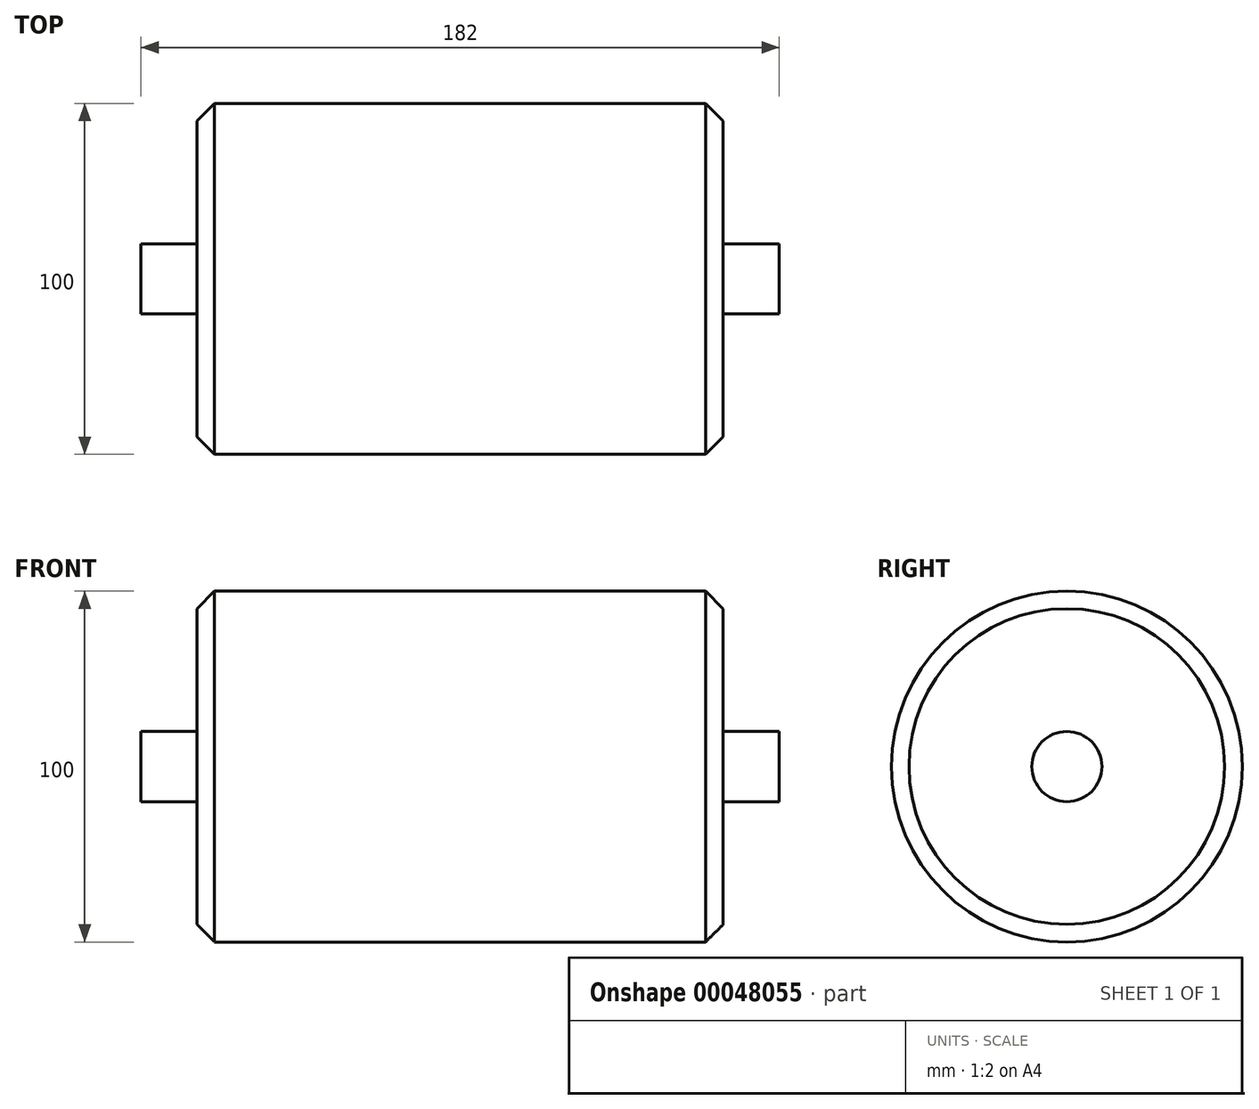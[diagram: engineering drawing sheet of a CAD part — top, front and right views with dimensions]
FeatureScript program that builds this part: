
annotation { "Feature Type Name" : "Feature", "Feature Type Description" : "" }
export const myFeature = defineFeature(function(context is Context, id is Id, definition is map)
    precondition{}
    {
        {
            var Q0;
            Q0=qCreatedBy(makeId("Right.planeOp"),FACE);
            var sketch = newSketch(context, id + "F0", { "sketchPlane" : qUnion([Q0])});
            skCircle(sketch, "E0", {"center": v(0, 0) * mm, "radius": 50 * mm});
            skCircle(sketch, "E1", {"center": v(0, 0) * mm, "radius": 10 * mm});
            skSolve(sketch);
        }
        {
            var Q0;
            Q0=makeQuery(id+"F0.imprint","IMPRINT",FACE,{"disambiguationData":[TD([[makeQuery(id+"F0.imprint","IMPRINT",EDGE,{"derivedFrom":sQuery(id+"F0.wireOp",EDGE,"E1")}),1.0]])]});
            extrude(context, id + "F1", {"entities" : qUnion([Q0]), "depth" : 16 * mm});
        }
        {
            var Q0;
            Q0=makeQuery(id+"F0.imprint","IMPRINT",FACE,{"disambiguationData":[TD([[makeQuery(id+"F0.imprint","IMPRINT",EDGE,{"derivedFrom":sQuery(id+"F0.wireOp",EDGE,"E1")}),-1.0]])]});
            var Q1;
            Q1=makeQuery(id+"F0.imprint","IMPRINT",FACE,{"disambiguationData":[TD([[makeQuery(id+"F0.imprint","IMPRINT",EDGE,{"derivedFrom":sQuery(id+"F0.wireOp",EDGE,"E0")}),1.0]])]});
            extrude(context, id + "F2", {"entities" : qUnion([Q0, Q1]), "operationType" : NewBodyOperationType.ADD, "oppositeDirection" : true, "depth" : 150 * mm});
        }
        {
            var Q0;
            Q0=makeQuery(id+"F2.opExtrude","CAP_EDGE",EDGE,{"disambiguationData":[OSD([sQuery(id+"F0.wireOp",EDGE,"E0")])],"isStart":true});
            chamfer(context, id + "F3", {"entities" : qUnion([Q0]), "chamferType" : ChamferType.OFFSET_ANGLE, "width" : 5 * mm, "oppositeDirection" : false, "angle" : 45 * degree, "tangentPropagation" : true});
        }
        {
            var Q0;
            Q0=makeQuery(id+"F2.opExtrude","CAP_EDGE",EDGE,{"disambiguationData":[OSD([sQuery(id+"F0.wireOp",EDGE,"E0")])],"isStart":false});
            chamfer(context, id + "F4", {"entities" : qUnion([Q0]), "chamferType" : ChamferType.OFFSET_ANGLE, "width" : 5 * mm, "oppositeDirection" : false, "angle" : 45 * degree, "tangentPropagation" : true});
        }
        {
            var Q0;
            Q0=makeQuery(id+"F0.imprint","IMPRINT",FACE,{"disambiguationData":[TD([[makeQuery(id+"F0.imprint","IMPRINT",EDGE,{"derivedFrom":sQuery(id+"F0.wireOp",EDGE,"E1")}),1.0]])]});
            extrude(context, id + "F5", {"entities" : qUnion([Q0]), "operationType" : NewBodyOperationType.ADD, "oppositeDirection" : true, "depth" : 166 * mm});
        }
    });
